# Revit family: DE_MEADRAIN_DM_CITY_Basic
name_source: partatom
category: Allgemeines Modell
revit_build: Autodesk Revit 2018 (Build: 20170223_1515(x64)
units: mm (PartAtom-declared; Revit-internal decimal feet)

## family parameters
Beim Laden mit Abzugskörper schneiden = Ja
Bemaßung runder Anschluss = Durchmesser verwenden
Gemeinsam genutzt = Nein
Kann Basisbauteil für Bewehrung sein = Nein
Raumberechnungspunkt = Nein
Teiletyp = Normal

## types (3) — shared parameters
Abdeckung = Gussrost
Außendurchmesser_Ablaufstutzen_Revisionselement = 200 mm  [stored 0.656168 ft]
B_Innendurchmesser_Ablaufstutzen = 180 mm  [stored 0.590551 ft]
Bauelement = Entwässerungsrinne Oberflächenwasser
Baustoff, Bettung/Fundament = gemäß Zeichnung und Einzelbeschreibung
Bauteil,Entwässerung = Entwässerungsrinne
Belastungsklasse Entwässerungsbauteil = D400
Beschreibung = Universal Entwässerungssystem aus Polymerbeton
Def Belastungsklasse_Rinne = D400
Eigung Entwässerungsbauteil = Für den Einatz in städtischen Bereichen
Einbautechnologie = Typ M
Fundament_Breite = 200 mm  [stored 0.656168 ft]
Gefälleart-/-Prozente Enwässerungsbauteil = Ohne Gefälle
Hersteller = MEA Bautechnik GmbH Geschäftsbereich MEA Water  Management
Hersteller und Typ- Ausschreibender gleichwertig = wie MEA Bautechnik GmbH, Modell MEADRAIN DM
IfcDescription = Universal Entwässerungssystem aus Polymerbeton
IfcExportAs = IfcWasteTerminalType
IfcExportType = USERDEFINED
Länge_Ablaufstutzen_Einlaufkasten = 194 mm
Länge_Ablaufstutzen_Revisionselement = 180 mm  [stored 0.590551 ft]
MEA Plannungshilfe = einschl. Fundament und Ummantelung
MEA-Belastungsklasse = D400
Modell = MEADRAIN DM
Produktwebsite = https://www.mea-group.com
Stirnplatte_Dicke = 3 mm  [stored 0.00984252 ft]
Technische Produktinformation = https://www.mea-group.com
Typ Entwässerungsbauteil = Beton
Typenkommentare = Für den Einatz in städtischen Bereichen
guid = cf6c1bd8-9bf4-4563-8c57-07955e2378ac

## per-type parameters (varying)
| type | Artikelnummer_Rinne | B_Breite | B_H01 | Breite_Rinnen | Höhe | MEA-Nennweite mm | Nennweite | hilfstype |
| DM CITY 1000 | 010712887 | 133 mm  [stored 0.436352 ft] | 225 mm  [stored 0.738189 ft] | 133 mm  [stored 0.436352 ft] | 225 mm  [stored 0.738189 ft] | 1000 | 100 mm  [stored 0.328084 ft] | 1 |
| DM CITY 1500 | 010712379 | 183 mm | 270 mm  [stored 0.885827 ft] | 183 mm | 270 mm  [stored 0.885827 ft] | 1500 | 150 mm  [stored 0.492126 ft] | 2 |
| DM CITY 2000 | 010712373 | 233 mm  [stored 0.764436 ft] | 330 mm | 233 mm  [stored 0.764436 ft] | 330 mm | 2000 | 200 mm  [stored 0.656168 ft] | 3 |

note: [stored X ft] marks values corroborated as IEEE doubles in the binary element streams (Revit-internal decimal feet)
